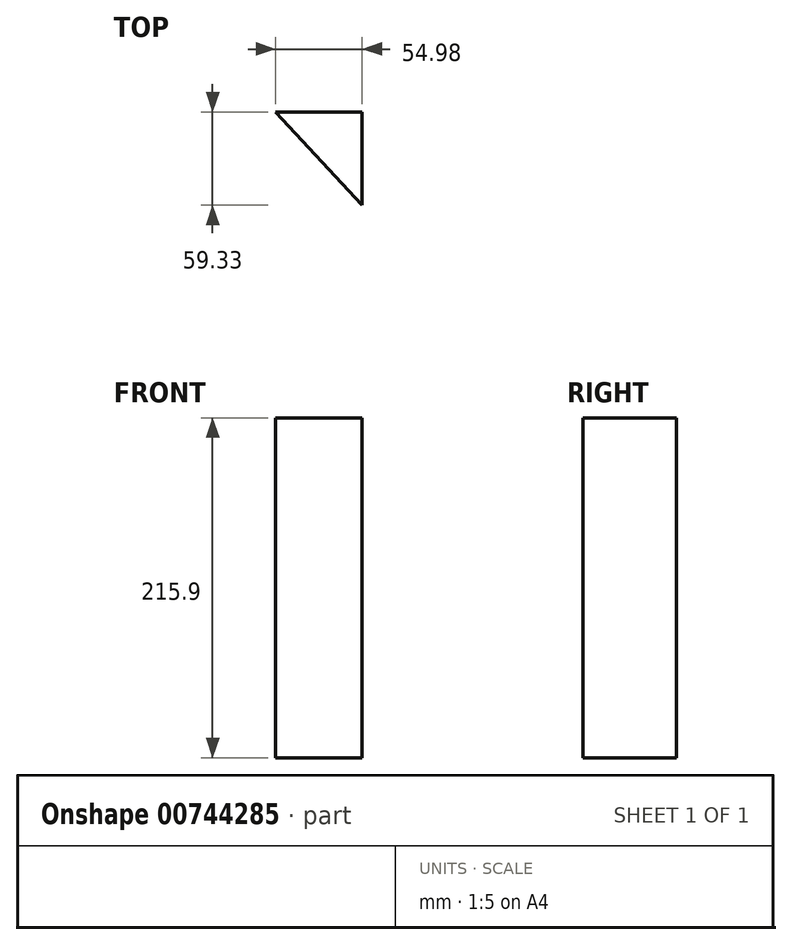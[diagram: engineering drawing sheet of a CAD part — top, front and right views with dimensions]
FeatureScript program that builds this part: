
annotation { "Feature Type Name" : "Feature", "Feature Type Description" : "" }
export const myFeature = defineFeature(function(context is Context, id is Id, definition is map)
    precondition{}
    {
        {
            var Q0;
            Q0=qCreatedBy(makeId("Top.planeOp"),FACE);
            var sketch = newSketch(context, id + "F0", { "sketchPlane" : qUnion([Q0])});
            skLineSegment(sketch, "E0", {"start": v(-27.8, 41.5) * mm, "end": v(27.18, 41.5) * mm});
            skLineSegment(sketch, "E1", {"start": v(27.18, 41.5) * mm, "end": v(27.18, -17.84) * mm});
            skLineSegment(sketch, "E2", {"start": v(27.18, -17.84) * mm, "end": v(-27.8, 41.5) * mm});
            skSolve(sketch);
        }
        {
            var Q0;
            Q0=makeQuery(id+"F0.imprint","IMPRINT",FACE,{"disambiguationData":[TD([[makeQuery(id+"F0.imprint","IMPRINT",EDGE,{"derivedFrom":sQuery(id+"F0.wireOp",EDGE,"E0")}),-1.0]])]});
            extrude(context, id + "F1", {"entities" : qUnion([Q0]), "depth" : 215.9 * mm, "offsetDistance" : 25.4 * mm});
        }
    });
